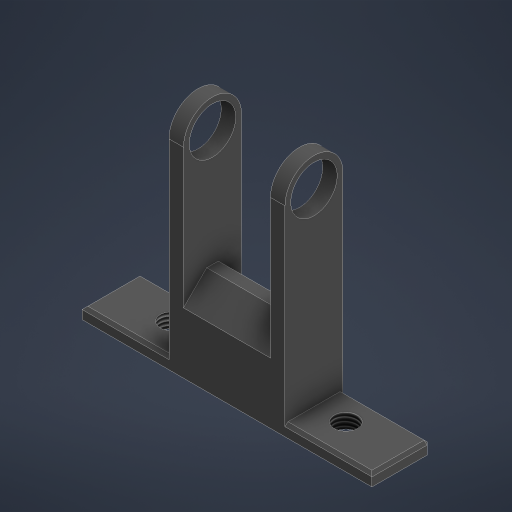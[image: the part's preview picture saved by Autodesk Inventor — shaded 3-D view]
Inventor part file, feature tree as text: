
AUTODESK INVENTOR PART (.ipt)
format: ipt  version: 2023 (Build 270158000, 158)  size: 256,000 bytes
history: native  units: mm
features: chamfer x3, sketch x3, hole x2, extrude x1, fillet x1, thread x1, mirror x1
ambient origin geometry x8: Origin, YZ Plane, XZ Plane, XY Plane, X Axis, Y Axis, Z Axis, Center Point
bodies: Body1 (feature_tree)
feature tree (12):
  extrude  "Extrusion3"  Depth=2.5mm
  fillet  "Fillet6"  Radius=15.0mm
  chamfer  "Chamfer1"  Distance=25.0mm
  hole  "Hole2"  [1 undecoded]
  thread  "Thread3"  [1 undecoded]
  mirror  "Mirror1"
  hole  "Hole3"  [1 undecoded]
  chamfer  "Chamfer2"  Distance=9.5mm
  chamfer  "Chamfer3"  Distance=4.0mm
  sketch  "Sketch4"  dims[d43=25.0mm d44=2.5mm d45=15.0mm]
  sketch  "Sketch5"  dims[d46=37.5mm]
  sketch  "Sketch6"  dims[d47=2.5mm d48=25.0mm d49=10.0mm d50=0.0mm d51=5.0mm d53=0.5mm d54=2.0mm d55=45.0deg d57=9.5mm d58=4.0mm d59=4.0mm d60=6.0mm d61=6.0mm d62=2.0mm d63=90.0deg d64=8.0mm d65=20.594885mm d66=2.5mm d67=0.0mm d68=8.0mm d69=6.0mm d70=4.0mm d71=2.0mm d72=90.0deg d73=8.0mm d74=20.594885mm d75=4.0mm d76=2.0mm d77=45.0deg d78=4.0mm d79=2.0mm d80=45.0deg]
note: 3 required parameter values undecoded (feature->parameter linkage not recoverable at this tier; creation-order binding heuristic only, values carry confidence <= 0.55)
